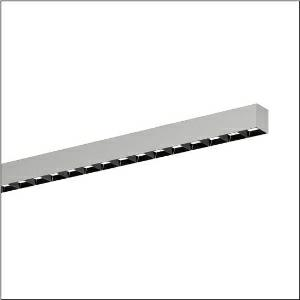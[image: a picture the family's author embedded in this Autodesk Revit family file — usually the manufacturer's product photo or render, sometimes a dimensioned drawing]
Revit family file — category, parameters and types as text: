
# Revit family: silica_r__21_51mx22dc3asb_7d31
name_source: partatom
category: Lighting Fixtures
units: mm (PartAtom-declared; Revit-internal decimal feet)

## family parameters
Cut with Voids When Loaded = No
Host = Face
Light Source = No
Part Type = Normal
Room Calculation Point = No
Round Connector Dimension = Use Diameter
Shared = No

## types (1)
- --- (1 x LED, 10800 lm, 69.2 W, 3000K)
    Apparent Load = 69 VA
    CIE Flux Codes = 86 100 100 100 100
    Color Rendering = 80
    Color Temperature = 3000K
    Default Elevation = 1800 mm
    Description = Silica® 21, office luminaire, primary light control with darklight reflector, of PMMA, black, CAT 2 (L<= 3000cd/m²), light emission: direct distribution, primary light characteristic: symmetric, installation type: surface-mounted, LED, rated luminous flux: 10.800lm, luminous efficacy: 156lm/W, light colour: 830, colour temperature: 3000K, control gear: DALI 2, with terminal, 3+2-pole, max. 2.5mm², mains connection: 220..240V, AC, 50/60Hz, rated input power: 69.2W, luminaire housing, of aluminium, metallic grey (RAL 9006), length: 3.004mm, width: 53mm, height: 53mm, protection rating (complete): IP20, insulation class (complete): insulation class I (protective earthing), certification: CE, permissible operating ambient temperature: 0..+35°C, standard: EN 50419, packaging unit: 1 piece
    Height = 53 mm
    Lamp = 1 x LED
    Lamp Light Flux = 10800 lm
    Lamp Power = 69.2 W
    Lamp count = 1
    Length = 3004 mm
    Luminous efficacy = 156 lm/W
    Manufacturer = Siteco
    ModVariant = No
    Model = 51MX22DC3ASB
    Mounting Place = Ceiling
    Mounting Type = Surface mounted
    Number of Poles = 1
    OnlyDefault = Yes
    Power Factor = 1
    Product Name = Silica® 21
    Product group = office luminaire | ceiling mounted
    ProductGroupID = 302
    Protection Class = Protection class I
    Protection Degree = IP 20
    RLX_Detail_Level = 1
    RLX_Emergency_Light_Flux = 0 lm
    RLX_Emergency_Type = 0
    RLX_Emergency_Type_DB = No
    RlxData = <blob elided: 63077 chars, md5=3949bfe2>
    Socket = socket
    Standby Power = 0 W
    System Light Flux = 10800 lm
    System Power = 69 W
    Type Comments = factory setting: luminous flux: 100 % | dim-lin: 254 | 392 mA
    Type Image = l_1335929.jpg
    URL = http://relux.com
    VarID = @adj_124504
    Voltage = 0 V
    Weight = 0.00 kg
    Width = 53 mm

## geometry (parser evidence)
native form markers: Blend x4, Sweep x12
no freeform markers — native parametric forms only
